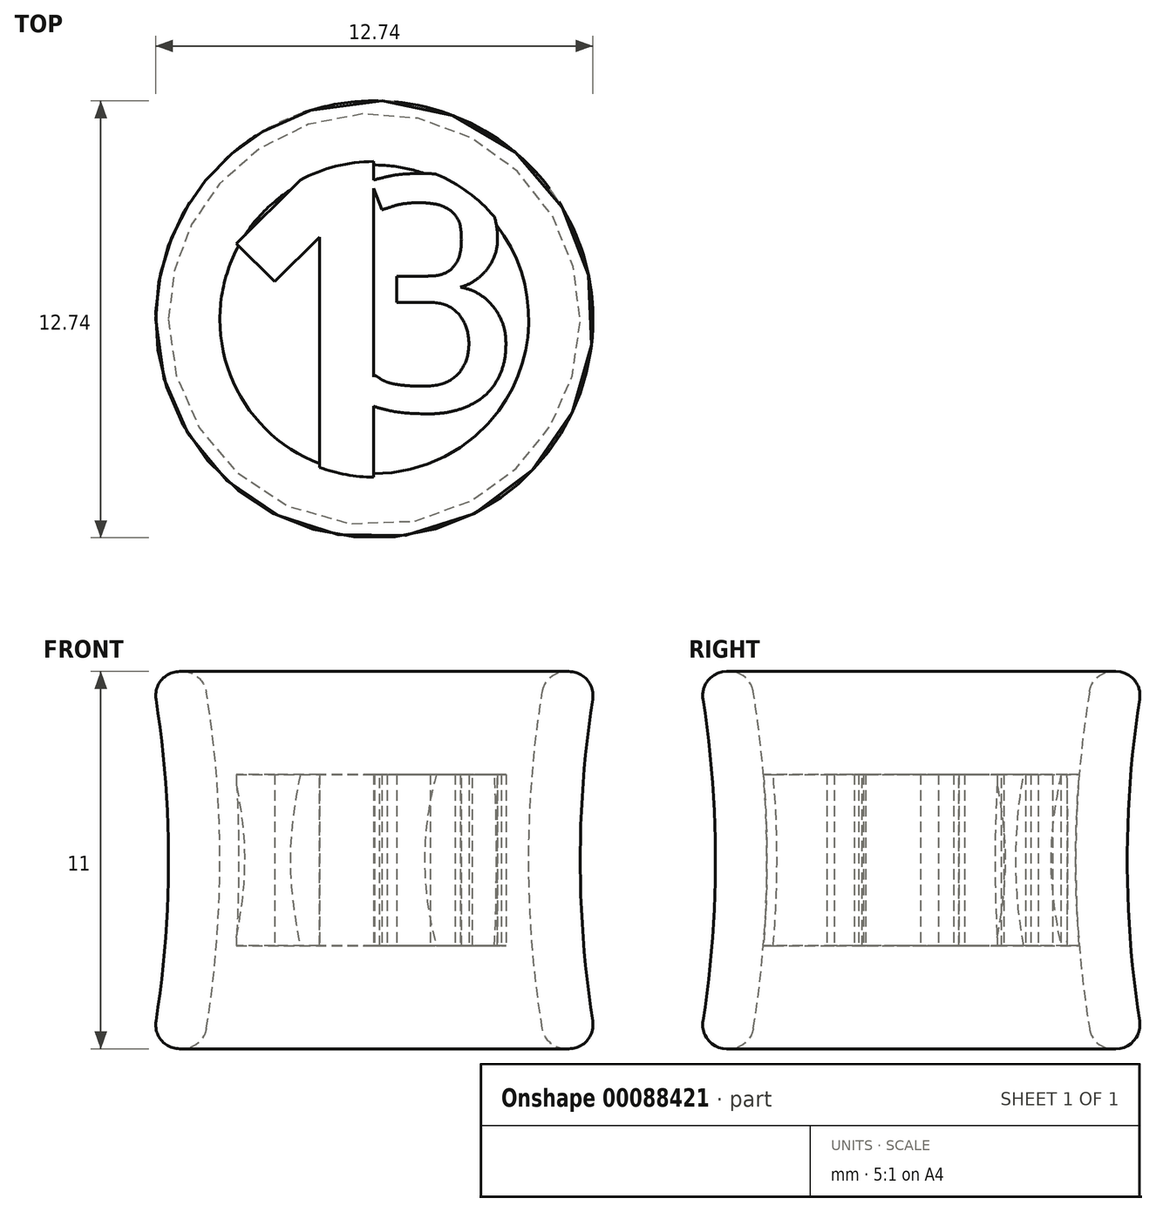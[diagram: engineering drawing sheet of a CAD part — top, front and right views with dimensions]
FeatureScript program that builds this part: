
annotation { "Feature Type Name" : "Feature", "Feature Type Description" : "" }
export const myFeature = defineFeature(function(context is Context, id is Id, definition is map)
    precondition{}
    {
        {
            var Q0;
            Q0=qCreatedBy(makeId("Right.planeOp"),FACE);
            var sketch = newSketch(context, id + "F0", { "sketchPlane" : qUnion([Q0])});
            skLineSegment(sketch, "E0", {"start": v(0, 0) * mm, "end": v(0, 5.87) * mm, "construction": true});
            skLineSegment(sketch, "E1", {"start": v(4.5, 0) * mm, "end": v(6, 0) * mm});
            skLineSegment(sketch, "E2", {"start": v(5, 5.5) * mm, "end": v(6.5, 5.5) * mm});
            skLineSegment(sketch, "E3", {"start": v(6, 0) * mm, "end": v(6, -1.82) * mm, "construction": true});
            skArc(sketch, "E4", {"start": v(6, 0) * mm, "mid": v(6.13, 2.76) * mm, "end": v(6.5, 5.5) * mm});
            skLineSegment(sketch, "E5", {"start": v(4.5, 0) * mm, "end": v(4.5, -1.86) * mm, "construction": true});
            skArc(sketch, "E6", {"start": v(4.5, 0) * mm, "mid": v(4.63, 2.76) * mm, "end": v(5, 5.5) * mm});
            skSolve(sketch);
        }
        {
            var Q0;
            Q0=makeQuery(id+"F0.imprint","IMPRINT",FACE,{"disambiguationData":[TD([[makeQuery(id+"F0.imprint","IMPRINT",EDGE,{"derivedFrom":sQuery(id+"F0.wireOp",EDGE,"E1")}),1.0]])]});
            var Q1;
            Q1=sQuery(id+"F0.wireOp",EDGE,"E0");
            revolve(context, id + "F1", {"entities" : qUnion([Q0]), "axis" : qUnion([Q1]), "revolveType" : RevolveType.FULL});
        }
        {
            var Q0;
            Q0=makeQuery(id+"F1.opRevolve","SWEPT_BODY",BODY,{"disambiguationData":[OSD([sQuery(id+"F0.wireOp",EDGE,"E1"),sQuery(id+"F0.wireOp",EDGE,"E2"),sQuery(id+"F0.wireOp",EDGE,"E4"),sQuery(id+"F0.wireOp",EDGE,"E6")])]});
            var Q1;
            Q1=qCreatedBy(makeId("Top.planeOp"),FACE);
            mirror(context, id + "F2", {"operationType" : NewBodyOperationType.ADD, "entities" : qUnion([Q0]), "mirrorPlane" : qUnion([Q1])});
        }
        {
            var Q0;
            Q0=makeQuery(id+"F1.opRevolve","SWEPT_FACE",FACE,{"disambiguationData":[OSD([sQuery(id+"F0.wireOp",EDGE,"E2")])]});
            var Q1;
            Q1=makeQuery(id+"F2.opPattern","COPY",FACE,{"derivedFrom":makeQuery(id+"F1.opRevolve","SWEPT_FACE",FACE,{"disambiguationData":[OSD([sQuery(id+"F0.wireOp",EDGE,"E2")])]}),"instanceName":"1"});
            fillet(context, id + "F3", {"entities" : qUnion([Q0, Q1]), "radius" : .7 * mm, "tangentPropagation" : true, "allowEdgeOverflow" : false});
        }
        {
            var Q0;
            Q0=qCreatedBy(makeId("Top.planeOp"),FACE);
            var sketch = newSketch(context, id + "F4", { "sketchPlane" : qUnion([Q0])});
            skText(sketch, "E7", { "text": "1", "fontName": "AllertaStencil-Regular.ttf"});
            skText(sketch, "E8", { "text": "2", "fontName": "AllertaStencil-Regular.ttf"});
            const initialGuessF4  = {"E7": [-0.00438, -0.0049, 1, 0, 0.00955], "E8": [-0.00113, -0.00283, 1, 0, 0.00693]};
            skSetInitialGuess(sketch, initialGuessF4);
            skSolve(sketch);
        }
        {
            var Q0;
            Q0=qCreatedBy(makeId("Top.planeOp"),FACE);
            var sketch = newSketch(context, id + "F5", { "sketchPlane" : qUnion([Q0])});
            skText(sketch, "E9", { "text": "1", "fontName": "AllertaStencil-Regular.ttf"});
            skText(sketch, "E10", { "text": "3", "fontName": "AllertaStencil-Regular.ttf"});
            const initialGuessF5  = {"E9": [-0.00439, -0.0049, 1, 0, 0.00953], "E10": [-0.00095, -0.00271, 1, 0, 0.00693]};
            skSetInitialGuess(sketch, initialGuessF5);
            skSolve(sketch);
        }
        {
            var Q0;
            Q0=makeQuery(id+"F5.imprint","IMPRINT",FACE,{"disambiguationData":[TD([[makeQuery(id+"F5.imprint","IMPRINT",EDGE,{"derivedFrom":sQuery(id+"F5.wireOp",EDGE,"E10.sketch_text.stroke-0")}),-1.0]])]});
            var Q1;
            {var subQ5=sQuery(id+"F5.wireOp",EDGE,"E9.sketch_text.stroke-0");Q1=makeQuery(id+"F5.imprint","IMPRINT",FACE,{"disambiguationData":[TD([[makeQuery(id+"F5.imprint","IMPRINT",EDGE,{"derivedFrom":subQ5}),-1.0]])]});}
            var Q2;
            {var subQ0=sQuery(id+"F5.wireOp",EDGE,"E10.sketch_text.stroke-11");var subQ1=sQuery(id+"F5.wireOp",EDGE,"E9.sketch_text.stroke-6");var subQ2=makeQuery(id+"F5.imprint","INTERSECT",VERTEX,{"derivedFrom":[subQ1,subQ0]});Q2=makeQuery(id+"F5.imprint","IMPRINT",FACE,{"disambiguationData":[TD([[makeQuery(id+"F5.imprint","IMPRINT",EDGE,{"disambiguationData":[TD([[subQ2,1.0]])],"derivedFrom":subQ1}),-1.0]])]});}
            var Q3;
            {var subQ0=sQuery(id+"F5.wireOp",EDGE,"E10.sketch_text.stroke-36");var subQ1=sQuery(id+"F5.wireOp",EDGE,"E9.sketch_text.stroke-6");var subQ2=makeQuery(id+"F5.imprint","INTERSECT",VERTEX,{"derivedFrom":[subQ1,subQ0]});Q3=makeQuery(id+"F5.imprint","IMPRINT",FACE,{"disambiguationData":[TD([[makeQuery(id+"F5.imprint","IMPRINT",EDGE,{"disambiguationData":[TD([[subQ2,-1.0]])],"derivedFrom":subQ1}),-1.0]])]});}
            extrude(context, id + "F6", {"entities" : qUnion([Q0, Q1, Q2, Q3]), "operationType" : NewBodyOperationType.ADD, "endBound" : BoundingType.SYMMETRIC, "depth" : 5 * mm});
        }
    });
